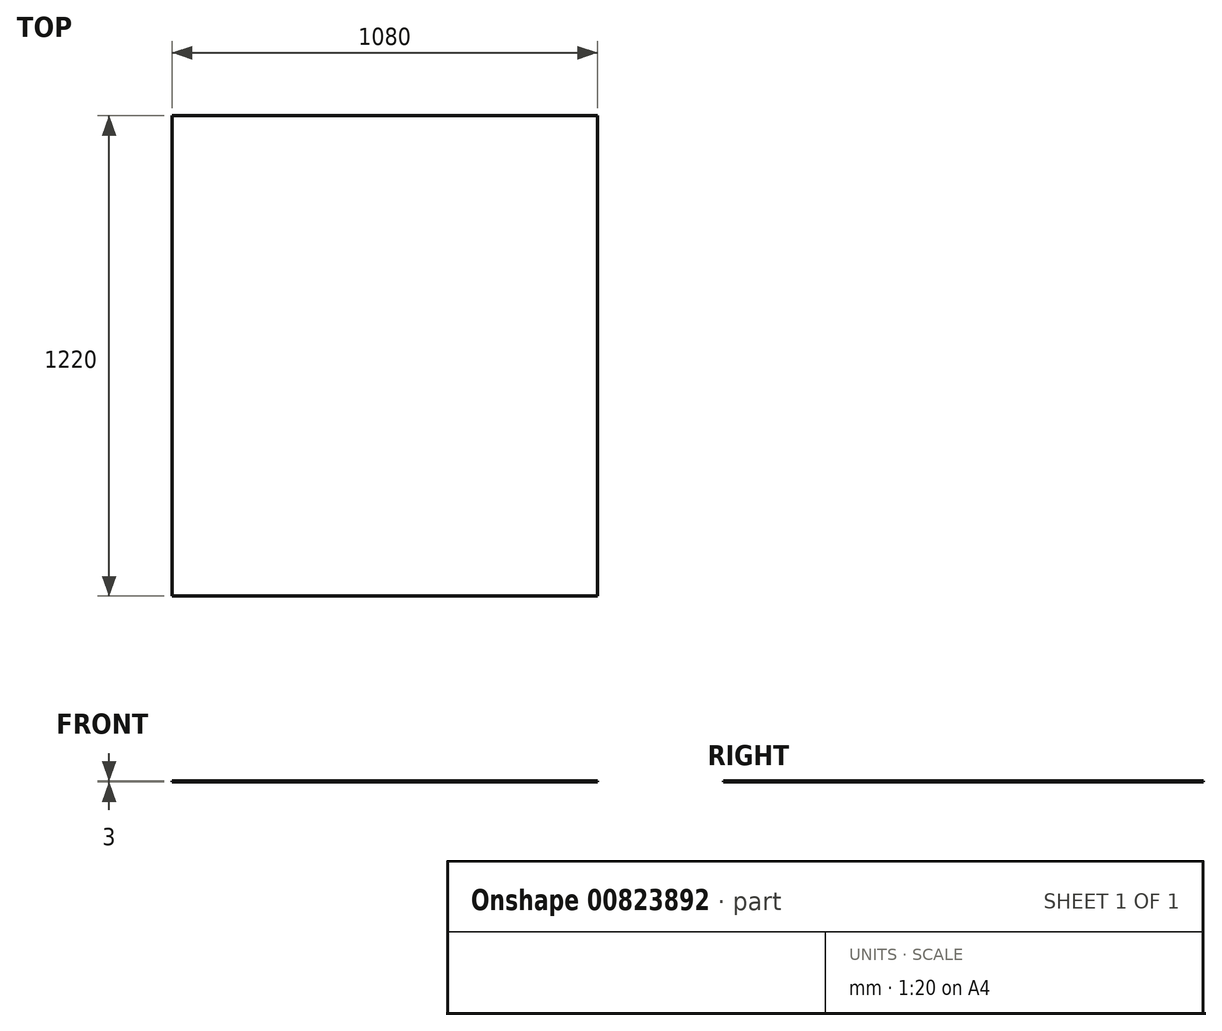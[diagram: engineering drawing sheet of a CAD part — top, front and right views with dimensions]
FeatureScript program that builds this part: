
annotation { "Feature Type Name" : "Feature", "Feature Type Description" : "" }
export const myFeature = defineFeature(function(context is Context, id is Id, definition is map)
    precondition{}
    {
        {
            var Q0;
            Q0=qCreatedBy(makeId("Top.planeOp"),FACE);
            var sketch = newSketch(context, id + "F0", { "sketchPlane" : qUnion([Q0])});
            skLineSegment(sketch, "E0.bottom", {"start": v(-540, 581.67) * mm, "end": v(540, 581.67) * mm});
            skLineSegment(sketch, "E0.top", {"start": v(-540, -638.33) * mm, "end": v(540, -638.33) * mm});
            skLineSegment(sketch, "E0.left", {"start": v(-540, 581.67) * mm, "end": v(-540, -638.33) * mm});
            skLineSegment(sketch, "E0.right", {"start": v(540, 581.67) * mm, "end": v(540, -638.33) * mm});
            skPoint(sketch, "E0.middle", {"position": v(0, -28.33) * mm});
            skSolve(sketch);
        }
        {
            var Q0;
            Q0=makeQuery(id+"F0.imprint","IMPRINT",FACE,{"disambiguationData":[TD([[makeQuery(id+"F0.imprint","IMPRINT",EDGE,{"derivedFrom":sQuery(id+"F0.wireOp",EDGE,"E0.bottom")}),-1.0]])]});
            extrude(context, id + "F1", {"entities" : qUnion([Q0]), "depth" : 3 * mm, "offsetDistance" : 25 * mm});
        }
    });
